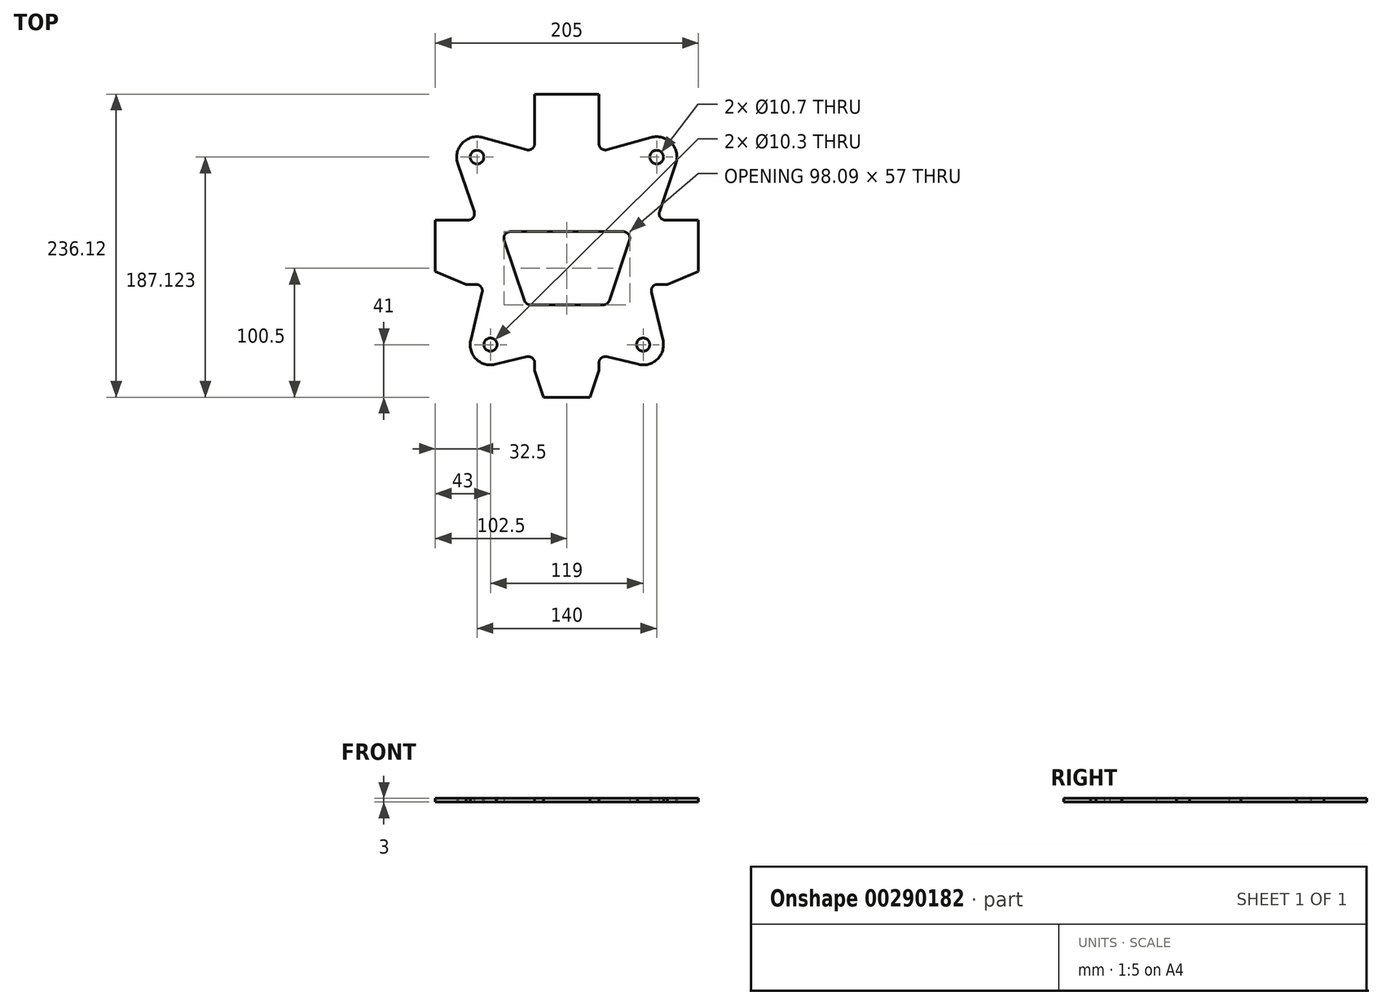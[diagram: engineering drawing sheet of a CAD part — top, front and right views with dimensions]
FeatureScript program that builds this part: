
annotation { "Feature Type Name" : "Feature", "Feature Type Description" : "" }
export const myFeature = defineFeature(function(context is Context, id is Id, definition is map)
    precondition{}
    {
        {
            var Q0;
            Q0=qCreatedBy(makeId("Top.planeOp"),FACE);
            var sketch = newSketch(context, id + "F0", { "sketchPlane" : qUnion([Q0])});
            skCircle(sketch, "E0", {"center": v(59.5, 0) * mm, "radius": 5.15 * mm});
            skCircle(sketch, "E1", {"center": v(70, 146.12) * mm, "radius": 5.35 * mm});
            skLineSegment(sketch, "E2", {"start": v(0, -20) * mm, "end": v(25, -20) * mm});
            skLineSegment(sketch, "E3", {"start": v(25, -20) * mm, "end": v(25, -14.34) * mm});
            skLineSegment(sketch, "E4", {"start": v(31.17, -9.48) * mm, "end": v(56.53, -15.57) * mm});
            skLineSegment(sketch, "E5", {"start": v(56.53, -15.57) * mm, "end": v(75, 3.28) * mm});
            skLineSegment(sketch, "E6", {"start": v(75, 3.28) * mm, "end": v(65.98, 40.83) * mm});
            skLineSegment(sketch, "E7", {"start": v(70.84, 47) * mm, "end": v(78.5, 47) * mm});
            skLineSegment(sketch, "E8", {"start": v(78.5, 47) * mm, "end": v(78.5, 97) * mm, "construction": true});
            skLineSegment(sketch, "E9", {"start": v(78.5, 97) * mm, "end": v(76.99, 97) * mm});
            skLineSegment(sketch, "E10", {"start": v(72.25, 103.61) * mm, "end": v(85.18, 141.55) * mm});
            skLineSegment(sketch, "E11", {"start": v(85.18, 141.55) * mm, "end": v(65.9, 161.44) * mm});
            skLineSegment(sketch, "E12", {"start": v(65.9, 161.44) * mm, "end": v(31.33, 151.87) * mm});
            skLineSegment(sketch, "E13", {"start": v(25, 156.7) * mm, "end": v(25, 195.12) * mm});
            skLineSegment(sketch, "E14", {"start": v(25, 195.12) * mm, "end": v(0, 195.12) * mm});
            skCircle(sketch, "E15", {"center": v(59.5, 0) * mm, "radius": 15.85 * mm});
            skCircle(sketch, "E16", {"center": v(70, 146.12) * mm, "radius": 15.85 * mm});
            skLineSegment(sketch, "E17.MirrorCS", {"start": v(-78.5, 97) * mm, "end": v(-76.99, 97) * mm});
            skLineSegment(sketch, "E18.MirrorCS", {"start": v(-25, -20) * mm, "end": v(-25, -14.34) * mm});
            skLineSegment(sketch, "E19.MirrorCS", {"start": v(-64.5, 47) * mm, "end": v(-64.5, 47) * mm});
            skLineSegment(sketch, "E20.MirrorCS", {"start": v(-64.5, 47) * mm, "end": v(-78.5, 47) * mm});
            skLineSegment(sketch, "E21.MirrorCS", {"start": v(-25, 156.7) * mm, "end": v(-25, 195.12) * mm});
            skLineSegment(sketch, "E22.MirrorCS", {"start": v(0, -20) * mm, "end": v(-25, -20) * mm});
            skCircle(sketch, "E23.MirrorC", {"center": v(-59.5, 0) * mm, "radius": 15.85 * mm});
            skLineSegment(sketch, "E24.MirrorCS", {"start": v(-85.18, 141.55) * mm, "end": v(-65.9, 161.44) * mm});
            skLineSegment(sketch, "E25.MirrorCS", {"start": v(-72.25, 103.61) * mm, "end": v(-85.18, 141.55) * mm});
            skLineSegment(sketch, "E26.MirrorCS", {"start": v(-56.53, -15.57) * mm, "end": v(-75, 3.28) * mm});
            skLineSegment(sketch, "E27.MirrorCS", {"start": v(-31.17, -9.48) * mm, "end": v(-56.53, -15.57) * mm});
            skLineSegment(sketch, "E28.MirrorCS", {"start": v(-75, 3.28) * mm, "end": v(-65.98, 40.83) * mm});
            skCircle(sketch, "E29.MirrorC", {"center": v(-70, 146.12) * mm, "radius": 15.85 * mm});
            skLineSegment(sketch, "E30.MirrorCS", {"start": v(-65.9, 161.44) * mm, "end": v(-31.33, 151.87) * mm});
            skCircle(sketch, "E31.MirrorC", {"center": v(-59.5, 0) * mm, "radius": 5.15 * mm});
            skLineSegment(sketch, "E32.MirrorCS", {"start": v(-25, 195.12) * mm, "end": v(0, 195.12) * mm});
            skCircle(sketch, "E33.MirrorC", {"center": v(-70, 146.12) * mm, "radius": 5.35 * mm});
            skLineSegment(sketch, "E34", {"start": v(0, 31) * mm, "end": v(28.4, 31) * mm});
            skLineSegment(sketch, "E35", {"start": v(33.14, 34.42) * mm, "end": v(48.8, 81.42) * mm});
            skLineSegment(sketch, "E36", {"start": v(44.06, 88) * mm, "end": v(0, 88) * mm});
            skPoint(sketch, "E37.visualSharp", {"position": v(32, 31) * mm});
            skArc(sketch, "E37.filletArc", {"start": v(28.4, 31) * mm, "mid": v(31.32, 31.94) * mm, "end": v(33.14, 34.42) * mm});
            skPoint(sketch, "E38.visualSharp", {"position": v(51, 88) * mm});
            skArc(sketch, "E38.filletArc", {"start": v(48.8, 81.42) * mm, "mid": v(48.12, 85.92) * mm, "end": v(44.06, 88) * mm});
            skArc(sketch, "E39.MirrorCS", {"start": v(-28.4, 31) * mm, "mid": v(-31.32, 31.94) * mm, "end": v(-33.14, 34.42) * mm});
            skLineSegment(sketch, "E40.MirrorCS", {"start": v(-44.06, 88) * mm, "end": v(0, 88) * mm});
            skPoint(sketch, "E41.MirrorP", {"position": v(-32, 31) * mm});
            skArc(sketch, "E42.MirrorCS", {"start": v(-48.8, 81.42) * mm, "mid": v(-48.12, 85.92) * mm, "end": v(-44.06, 88) * mm});
            skPoint(sketch, "E43.MirrorP", {"position": v(-51, 88) * mm});
            skLineSegment(sketch, "E44.MirrorCS", {"start": v(0, 31) * mm, "end": v(-28.4, 31) * mm});
            skLineSegment(sketch, "E45.MirrorCS", {"start": v(-33.14, 34.42) * mm, "end": v(-48.8, 81.42) * mm});
            skLineSegment(sketch, "E46", {"start": v(25, -20) * mm, "end": v(18, -41) * mm});
            skLineSegment(sketch, "E47", {"start": v(18, -41) * mm, "end": v(0, -41) * mm});
            skLineSegment(sketch, "E48.MirrorCS", {"start": v(-18, -41) * mm, "end": v(0, -41) * mm});
            skLineSegment(sketch, "E49.MirrorCS", {"start": v(-25, -20) * mm, "end": v(-18, -41) * mm});
            skPoint(sketch, "E50.visualSharp", {"position": v(25, -8) * mm});
            skArc(sketch, "E50.filletArc", {"start": v(31.17, -9.48) * mm, "mid": v(26.9, -10.42) * mm, "end": v(25, -14.34) * mm});
            skPoint(sketch, "E51.visualSharp", {"position": v(-25, -8) * mm});
            skArc(sketch, "E51.filletArc", {"start": v(-25, -14.34) * mm, "mid": v(-26.9, -10.42) * mm, "end": v(-31.17, -9.48) * mm});
            skLineSegment(sketch, "E52", {"start": v(78.5, 47) * mm, "end": v(102.5, 57) * mm});
            skLineSegment(sketch, "E53", {"start": v(102.5, 57) * mm, "end": v(102.5, 97) * mm});
            skLineSegment(sketch, "E54", {"start": v(102.5, 97) * mm, "end": v(78.5, 97) * mm});
            skLineSegment(sketch, "E55.MirrorCS", {"start": v(-70.84, 47) * mm, "end": v(-78.5, 47) * mm});
            skLineSegment(sketch, "E56.MirrorCS", {"start": v(-78.5, 97) * mm, "end": v(-70, 97) * mm});
            skLineSegment(sketch, "E57.MirrorCS", {"start": v(-102.5, 57) * mm, "end": v(-102.5, 97) * mm});
            skLineSegment(sketch, "E58.MirrorCS", {"start": v(-102.5, 97) * mm, "end": v(-78.5, 97) * mm});
            skLineSegment(sketch, "E59.MirrorCS", {"start": v(-78.5, 47) * mm, "end": v(-102.5, 57) * mm});
            skLineSegment(sketch, "E60.MirrorCS", {"start": v(-78.5, 47) * mm, "end": v(-78.5, 97) * mm, "construction": true});
            skPoint(sketch, "E61.visualSharp", {"position": v(64.5, 47) * mm});
            skArc(sketch, "E61.filletArc", {"start": v(70.84, 47) * mm, "mid": v(66.92, 45.1) * mm, "end": v(65.98, 40.83) * mm});
            skPoint(sketch, "E62.visualSharp", {"position": v(70, 97) * mm});
            skArc(sketch, "E62.filletArc", {"start": v(72.25, 103.61) * mm, "mid": v(72.92, 99.09) * mm, "end": v(76.99, 97) * mm});
            skPoint(sketch, "E63.visualSharp", {"position": v(-64.5, 47) * mm});
            skArc(sketch, "E63.filletArc", {"start": v(-65.98, 40.83) * mm, "mid": v(-66.92, 45.1) * mm, "end": v(-70.84, 47) * mm});
            skPoint(sketch, "E64.visualSharp", {"position": v(-70, 97) * mm});
            skArc(sketch, "E64.filletArc", {"start": v(-76.99, 97) * mm, "mid": v(-72.92, 99.09) * mm, "end": v(-72.25, 103.61) * mm});
            skPoint(sketch, "E65.visualSharp", {"position": v(25, 150.12) * mm});
            skArc(sketch, "E65.filletArc", {"start": v(25, 156.7) * mm, "mid": v(26.97, 152.71) * mm, "end": v(31.33, 151.87) * mm});
            skPoint(sketch, "E66.visualSharp", {"position": v(-25, 150.12) * mm});
            skArc(sketch, "E66.filletArc", {"start": v(-31.33, 151.87) * mm, "mid": v(-26.97, 152.71) * mm, "end": v(-25, 156.7) * mm});
            skLineSegment(sketch, "E67", {"start": v(25, 162.8) * mm, "end": v(-25, 162.8) * mm, "construction": true});
            skLineSegment(sketch, "E68", {"start": v(-25, -14) * mm, "end": v(25, -14) * mm, "construction": true});
            skSolve(sketch);
        }
        {
            var Q0;
            Q0=qSketchRegion(id+"F0",true);
            var Q1;
            {var subQ0=sQuery(id+"F0.wireOp",EDGE,"E187.MirrorCS");var subQ1=sQuery(id+"F0.wireOp",EDGE,"OiVEDE76-u2D4-DFK1-LXFl-u1fkFTkjrzRN");var subQ2=makeQuery(id+"F0.imprint","INTERSECT",VERTEX,{"derivedFrom":[subQ1,subQ0]});Q1=makeQuery(id+"F0.imprint","IMPRINT",FACE,{"disambiguationData":[TD([[makeQuery(id+"F0.imprint","IMPRINT",EDGE,{"disambiguationData":[TD([[subQ2,1.0]])],"derivedFrom":subQ1}),-1.0]])]});}
            extrude(context, id + "F1", {"entities" : qUnion([Q0, Q1]), "depth" : 3 * mm});
        }
        {
            var Q0;
            Q0 = qSketchRegion(id + "F0", true);
            extrude(context, id + "F2", {"entities" : qUnion([Q0]), "operationType" : NewBodyOperationType.ADD, "depth" : 3 * mm});
        }
    });
